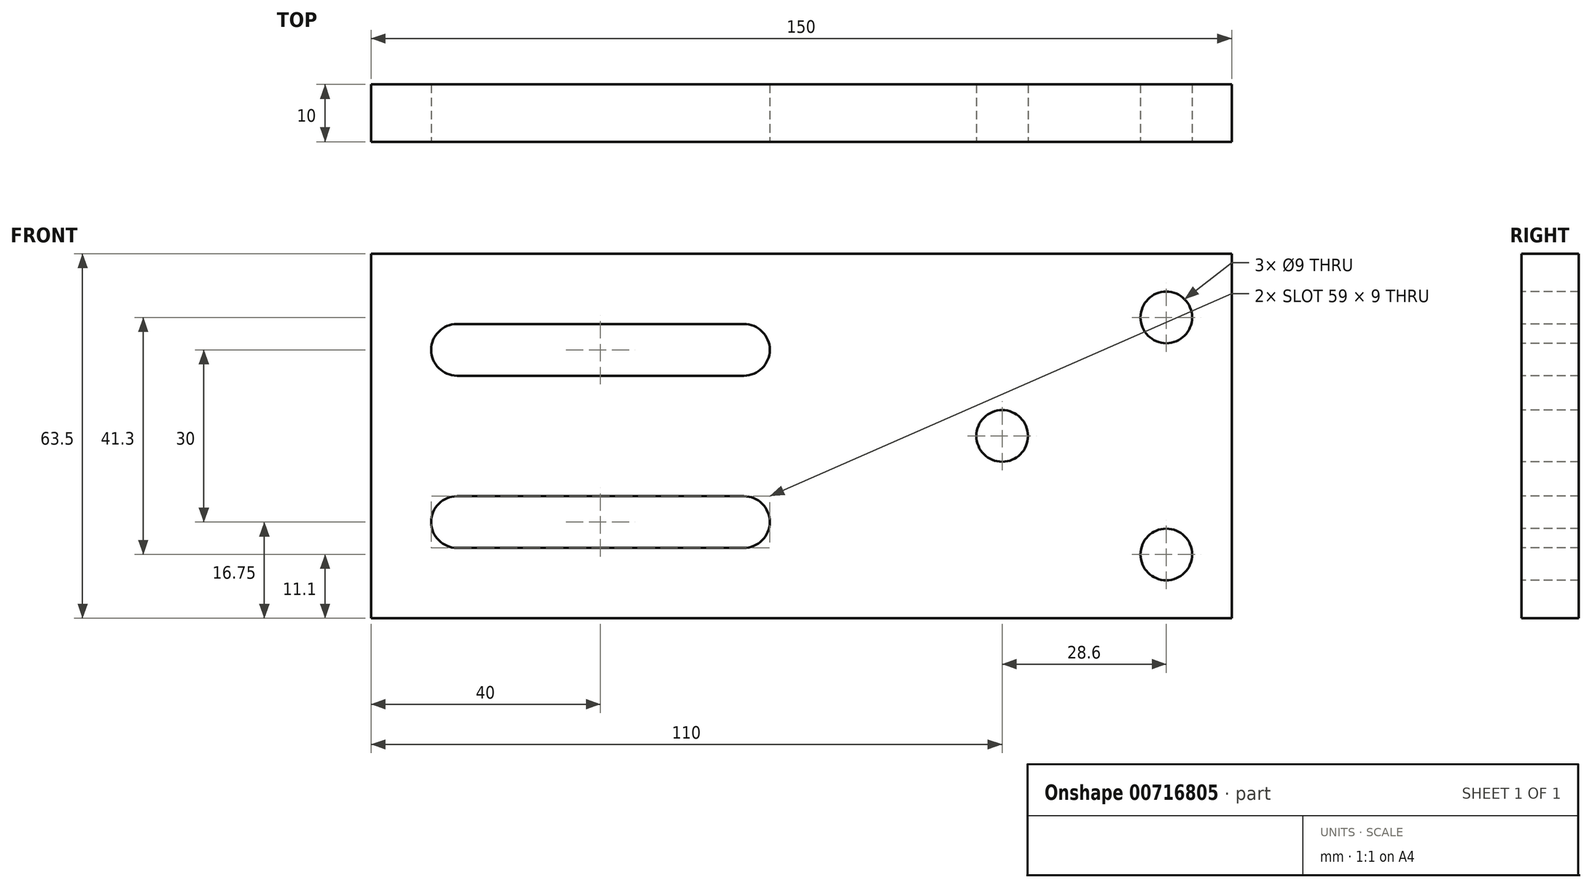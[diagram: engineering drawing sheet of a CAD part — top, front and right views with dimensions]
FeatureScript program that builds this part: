
annotation { "Feature Type Name" : "Feature", "Feature Type Description" : "" }
export const myFeature = defineFeature(function(context is Context, id is Id, definition is map)
    precondition{}
    {
        {
            var Q0;
            Q0=qCreatedBy(makeId("Front.planeOp"),FACE);
            var sketch = newSketch(context, id + "F0", { "sketchPlane" : qUnion([Q0])});
            skLineSegment(sketch, "E0.bottom", {"start": v(-75, 31.75) * mm, "end": v(75, 31.75) * mm});
            skLineSegment(sketch, "E0.top", {"start": v(-75, -31.75) * mm, "end": v(75, -31.75) * mm});
            skLineSegment(sketch, "E0.left", {"start": v(-75, 31.75) * mm, "end": v(-75, -31.75) * mm});
            skLineSegment(sketch, "E0.right", {"start": v(75, 31.75) * mm, "end": v(75, -31.75) * mm});
            skPoint(sketch, "E0.middle", {"position": v(0, 0) * mm});
            skSolve(sketch);
        }
        {
            var Q0;
            Q0 = qSketchRegion(id + "F0", true);
            extrude(context, id + "F1", {"entities" : qUnion([Q0]), "endBound" : BoundingType.SYMMETRIC, "depth" : 10 * mm, "offsetDistance" : 25 * mm});
        }
        {
            var Q0;
            Q0=makeQuery(id+"F1.opExtrude","CAP_FACE",FACE,{"disambiguationData":[OSD([sQuery(id+"F0.wireOp",EDGE,"E0.bottom"),sQuery(id+"F0.wireOp",EDGE,"E0.top"),sQuery(id+"F0.wireOp",EDGE,"E0.left"),sQuery(id+"F0.wireOp",EDGE,"E0.right")])],"isStart":false});
            var sketch = newSketch(context, id + "F2", { "sketchPlane" : qUnion([Q0])});
            skLineSegment(sketch, "E1", {"start": v(-60, 15) * mm, "end": v(-10, 15) * mm, "construction": true});
            skArc(sketch, "E2.0.startCap", {"start": v(-60, 10.5) * mm, "mid": v(-64.5, 15) * mm, "end": v(-60, 19.5) * mm});
            skArc(sketch, "E2.0.endCap", {"start": v(-10, 19.5) * mm, "mid": v(-5.5, 15) * mm, "end": v(-10, 10.5) * mm});
            skLineSegment(sketch, "E2.0.left", {"start": v(-60, 19.5) * mm, "end": v(-10, 19.5) * mm});
            skLineSegment(sketch, "E2.0.right", {"start": v(-60, 10.5) * mm, "end": v(-10, 10.5) * mm});
            skLineSegment(sketch, "E3", {"start": v(-60, -15) * mm, "end": v(-10, -15) * mm, "construction": true});
            skArc(sketch, "E4.0.startCap", {"start": v(-60, -19.5) * mm, "mid": v(-64.5, -15) * mm, "end": v(-60, -10.5) * mm});
            skArc(sketch, "E4.0.endCap", {"start": v(-10, -10.5) * mm, "mid": v(-5.5, -15) * mm, "end": v(-10, -19.5) * mm});
            skLineSegment(sketch, "E4.0.left", {"start": v(-60, -10.5) * mm, "end": v(-10, -10.5) * mm});
            skLineSegment(sketch, "E4.0.right", {"start": v(-60, -19.5) * mm, "end": v(-10, -19.5) * mm});
            skSolve(sketch);
        }
        {
            var Q0;
            Q0 = qSketchRegion(id + "F2", true);
            extrude(context, id + "F3", {"entities" : qUnion([Q0]), "operationType" : NewBodyOperationType.REMOVE, "endBound" : BoundingType.THROUGH_ALL, "oppositeDirection" : true, "depth" : 25 * mm, "offsetDistance" : 25 * mm});
        }
        {
            var Q0;
            Q0=makeQuery(id+"F1.opExtrude","CAP_FACE",FACE,{"disambiguationData":[OSD([sQuery(id+"F0.wireOp",EDGE,"E0.bottom"),sQuery(id+"F0.wireOp",EDGE,"E0.top"),sQuery(id+"F0.wireOp",EDGE,"E0.left"),sQuery(id+"F0.wireOp",EDGE,"E0.right")])],"isStart":false});
            var sketch = newSketch(context, id + "F4", { "sketchPlane" : qUnion([Q0])});
            skPoint(sketch, "E5", {"position": v(35, 0) * mm});
            skPoint(sketch, "E6", {"position": v(63.6, 20.65) * mm});
            skPoint(sketch, "E7", {"position": v(63.6, -20.65) * mm});
            skLineSegment(sketch, "E8", {"start": v(63.6, 20.65) * mm, "end": v(63.6, -20.65) * mm, "construction": true});
            skLineSegment(sketch, "E9", {"start": v(63.6, 0) * mm, "end": v(35, 0) * mm, "construction": true});
            skSolve(sketch);
        }
        {
            var Q0;
            Q0=sQuery(id+"F4.wireOp",VERTEX,"E5");
            var Q1;
            Q1=sQuery(id+"F4.wireOp",VERTEX,"E6");
            var Q2;
            Q2=sQuery(id+"F4.wireOp",VERTEX,"E7");
            var Q3;
            Q3=makeQuery(id+"F1.opExtrude","SWEPT_BODY",BODY,{"disambiguationData":[OSD([sQuery(id+"F0.wireOp",EDGE,"E0.bottom"),sQuery(id+"F0.wireOp",EDGE,"E0.top"),sQuery(id+"F0.wireOp",EDGE,"E0.left"),sQuery(id+"F0.wireOp",EDGE,"E0.right")])]});
            hole(context, id + "F5", {"style" : HoleStyle.SIMPLE, "endStyle" : HoleEndStyle.BLIND, "standardTappedOrClearance" : lookupTablePath({ "standard" : "ISO", "engagement" : "75%", "pitch" : "1 mm", "size" : "M10", "type" : "Tapped" }), "standardBlindInLast" : lookupTablePath({ "standard" : "ISO", "engagement" : "75%", "pitch" : "1 mm", "size" : "M10", "type" : "Tapped" }), "holeDiameter" : 9 * mm, "majorDiameter" : 10 * mm, "showTappedDepth" : true, "holeDepth" : 18 * mm, "isTappedThrough" : true, "tappedDepth" : 15 * mm, "tapClearance" : 3, "startFromSketch" : true, "locations" : qUnion([Q0, Q1, Q2]), "scope" : qUnion([Q3])});
        }
    });
